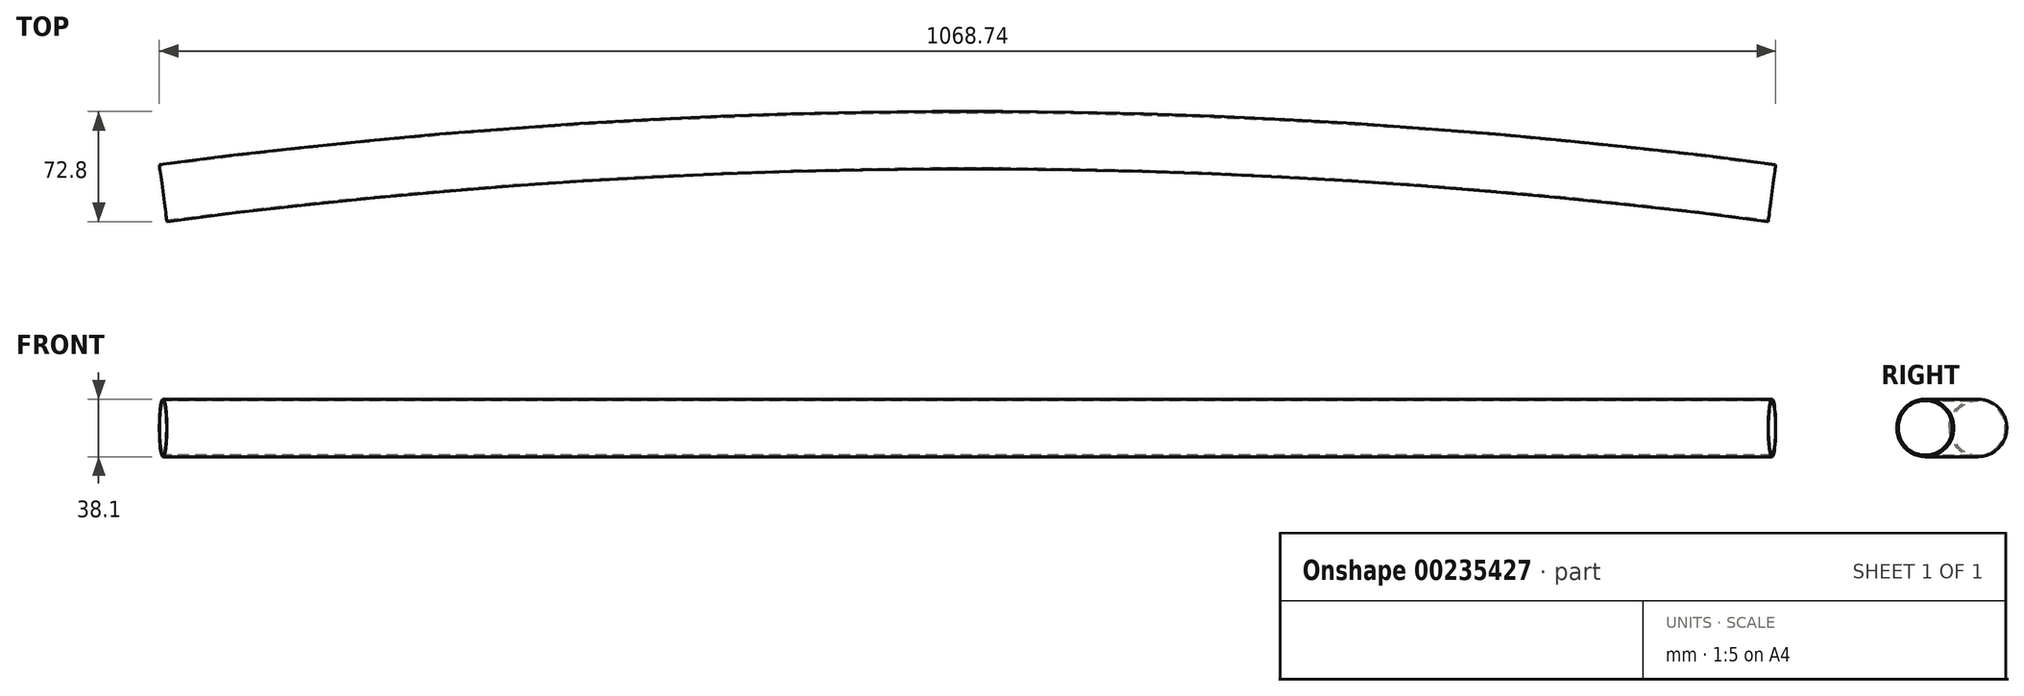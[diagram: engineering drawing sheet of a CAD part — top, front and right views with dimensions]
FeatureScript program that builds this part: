
annotation { "Feature Type Name" : "Feature", "Feature Type Description" : "" }
export const myFeature = defineFeature(function(context is Context, id is Id, definition is map)
    precondition{}
    {
        {
            var Q0;
            Q0=qCreatedBy(makeId("Top.planeOp"),FACE);
            var sketch = newSketch(context, id + "F0", { "sketchPlane" : qUnion([Q0])});
            skArc(sketch, "E0", {"start": v(531.88, 0) * mm, "mid": v(0, 34.86) * mm, "end": v(-531.88, 0) * mm});
            skLineSegment(sketch, "E1", {"start": v(-531.88, 0) * mm, "end": v(531.88, 0) * mm, "construction": true});
            skLineSegment(sketch, "E2", {"start": v(-531.88, 0) * mm, "end": v(0, -4040.02) * mm, "construction": true});
            skLineSegment(sketch, "E3", {"start": v(0, -4040.02) * mm, "end": v(531.88, 0) * mm, "construction": true});
            skSolve(sketch);
        }
        {
            var Q0;
            Q0=sQuery(id+"F0.wireOp",VERTEX,"E2.start");
            var Q1;
            Q1=sQuery(id+"F0.wireOp",EDGE,"E0");
            cPlane(context, id + "F1", {"entities" : qUnion([Q0, Q1]), "cplaneType" : CPlaneType.CURVE_POINT, "offset" : 25.4 * mm, "width" : 152.4 * mm, "height" : 152.4 * mm});
        }
        {
            var Q0;
            Q0=qCreatedBy(id+"F1.planeOp",FACE);
            var sketch = newSketch(context, id + "F2", { "sketchPlane" : qUnion([Q0])});
            skCircle(sketch, "E4", {"center": v(-69.42, 0) * mm, "radius": 19.05 * mm});
            skCircle(sketch, "E5", {"center": v(-69.42, 0) * mm, "radius": 18.05 * mm});
            skSolve(sketch);
        }
        {
            var Q0;
            Q0=makeQuery(id+"F2.imprint","IMPRINT",FACE,{"disambiguationData":[TD([[makeQuery(id+"F2.imprint","IMPRINT",EDGE,{"derivedFrom":sQuery(id+"F2.wireOp",EDGE,"E4")}),1.0]])]});
            var Q1;
            Q1=sQuery(id+"F0.wireOp",EDGE,"E0");
            sweep(context, id + "F3", {"profiles" : qUnion([Q0]), "path" : qUnion([Q1])});
        }
    });
